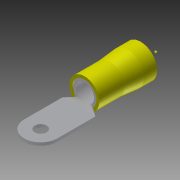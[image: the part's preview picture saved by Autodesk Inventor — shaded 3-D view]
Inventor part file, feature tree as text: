
AUTODESK INVENTOR PART (.ipt)
format: ipt  version: 2011 (Build 150239000, 239)  size: 135,680 bytes
history: native  units: mm
features: other x4, plane x2, imported_body x1, sketch x1
ambient origin geometry x8: Origin, YZ Plane, XZ Plane, XY Plane, X Axis, Y Axis, Z Axis, Center Point
bodies: Solid1 (feature_tree)
feature tree (8):
  imported_body  "Base1"
  sketch  "Sketch1"  dims[d0=3.175mm d1=6.35mm]
  other  "Work Point2"
  other  "Work Point3"
  plane  "Work Plane1"
  other  "Work Axis1"
  plane  "Work Plane2"
  other  "Work Axis2"
